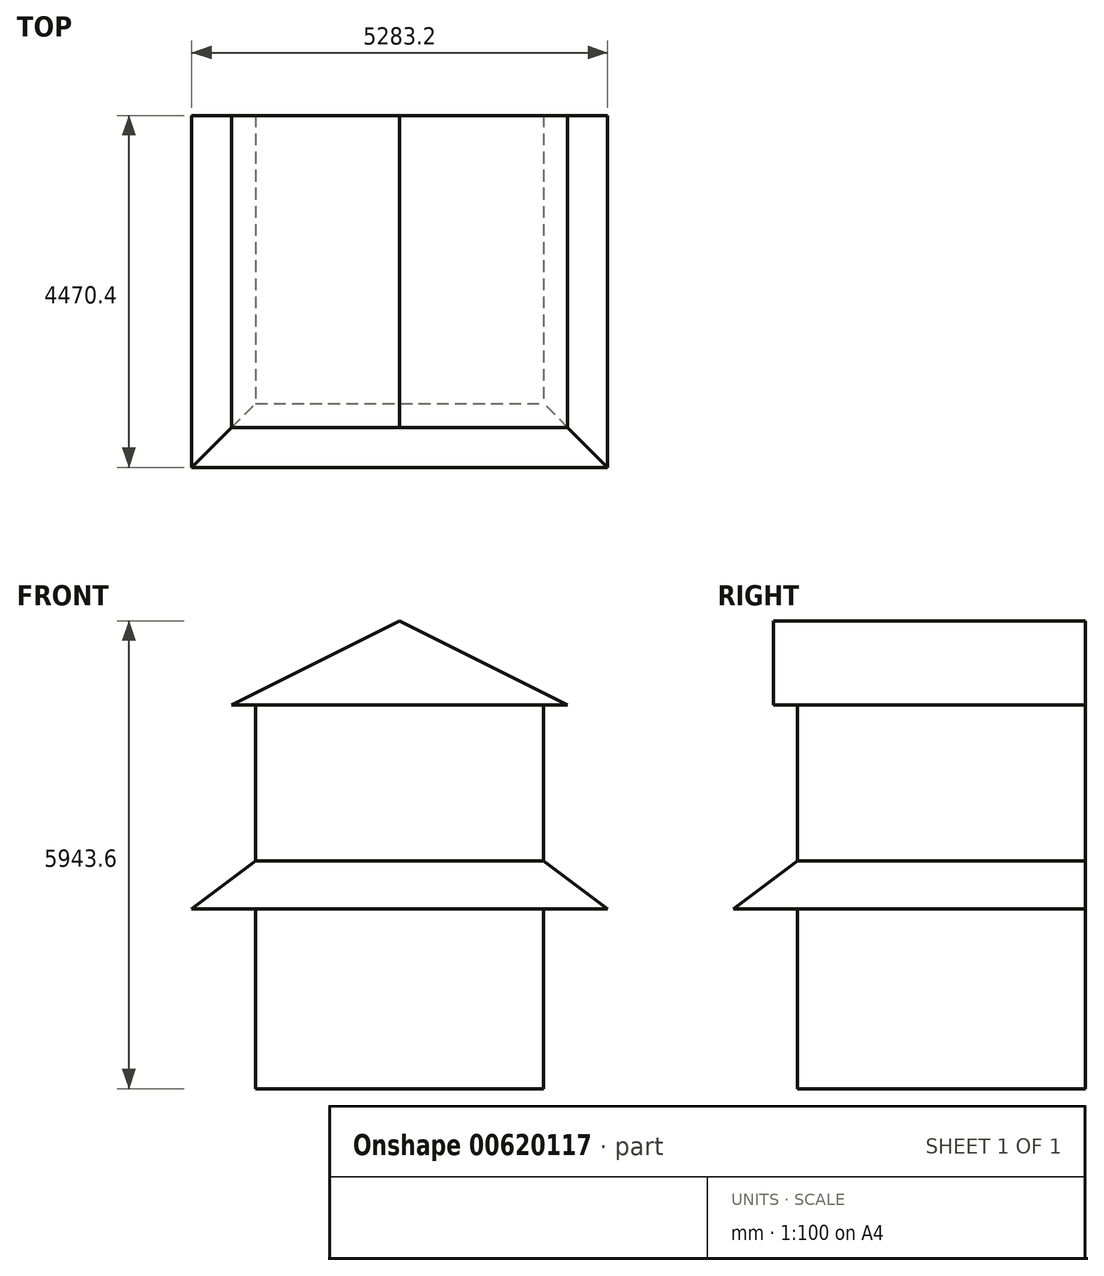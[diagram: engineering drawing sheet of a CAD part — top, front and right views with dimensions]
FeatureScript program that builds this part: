
annotation { "Feature Type Name" : "Feature", "Feature Type Description" : "" }
export const myFeature = defineFeature(function(context is Context, id is Id, definition is map)
    precondition{}
    {
        {
            var Q0;
            Q0=qCreatedBy(makeId("Top.planeOp"),FACE);
            var sketch = newSketch(context, id + "F0", { "sketchPlane" : qUnion([Q0])});
            skLineSegment(sketch, "E0.bottom", {"start": v(-1828.8, 1828.8) * mm, "end": v(1828.8, 1828.8) * mm});
            skLineSegment(sketch, "E0.top", {"start": v(-1828.8, -1828.8) * mm, "end": v(1828.8, -1828.8) * mm});
            skLineSegment(sketch, "E0.left", {"start": v(-1828.8, 1828.8) * mm, "end": v(-1828.8, -1828.8) * mm});
            skLineSegment(sketch, "E0.right", {"start": v(1828.8, 1828.8) * mm, "end": v(1828.8, -1828.8) * mm});
            skLineSegment(sketch, "E1", {"start": v(1828.8, 1828.8) * mm, "end": v(-1828.8, -1828.8) * mm, "construction": true});
            skSolve(sketch);
        }
        {
            var Q0;
            Q0=makeQuery(id+"F0.imprint","IMPRINT",FACE,{"disambiguationData":[TD([[makeQuery(id+"F0.imprint","IMPRINT",EDGE,{"derivedFrom":sQuery(id+"F0.wireOp",EDGE,"E0.bottom")}),-1.0]])]});
            extrude(context, id + "F1", {"entities" : qUnion([Q0]), "depth" : 4876.8 * mm, "offsetDistance" : 25.4 * mm});
        }
        {
            var Q0;
            Q0=makeQuery(id+"F1.opExtrude","SWEPT_FACE",FACE,{"disambiguationData":[OSD([sQuery(id+"F0.wireOp",EDGE,"E0.top")])]});
            var sketch = newSketch(context, id + "F2", { "sketchPlane" : qUnion([Q0])});
            skLineSegment(sketch, "E2.0", {"start": v(-2133.6, 4876.8) * mm, "end": v(2133.6, 4876.8) * mm});
            skLineSegment(sketch, "E3", {"start": v(-2133.6, 4876.8) * mm, "end": v(0, 5943.6) * mm});
            skLineSegment(sketch, "E4", {"start": v(0, 5943.6) * mm, "end": v(2133.6, 4876.8) * mm});
            skSolve(sketch);
        }
        {
            var Q0;
            Q0 = qSketchRegion(id + "F2", true);
            var Q1;
            Q1=makeQuery(id+"F1.opExtrude","SWEPT_FACE",FACE,{"disambiguationData":[OSD([sQuery(id+"F0.wireOp",EDGE,"E0.bottom")])]});
            extrude(context, id + "F3", {"entities" : qUnion([Q0]), "operationType" : NewBodyOperationType.ADD, "depth" : 304.8 * mm, "offsetDistance" : 25.4 * mm, "hasSecondDirection" : true, "secondDirectionBound" : BoundingType.UP_TO_SURFACE, "secondDirectionOppositeDirection" : true, "secondDirectionDepth" : 25.4 * mm, "secondDirectionBoundEntityFace" : qUnion([Q1])});
        }
        {
            var Q0;
            Q0=makeQuery(id+"F1.opExtrude","SWEPT_FACE",FACE,{"disambiguationData":[OSD([sQuery(id+"F0.wireOp",EDGE,"E0.top")])]});
            var sketch = newSketch(context, id + "F4", { "sketchPlane" : qUnion([Q0])});
            skLineSegment(sketch, "E5", {"start": v(-1828.8, 2895.6) * mm, "end": v(-1828.8, 2286) * mm});
            skLineSegment(sketch, "E6", {"start": v(-1828.8, 2286) * mm, "end": v(-2641.6, 2286) * mm});
            skLineSegment(sketch, "E7", {"start": v(-2641.6, 2286) * mm, "end": v(-1828.8, 2895.6) * mm});
            skLineSegment(sketch, "E8", {"start": v(0, 0) * mm, "end": v(0, 3018.86) * mm, "construction": true});
            skPoint(sketch, "E8.endSnap0", {"position": v(0, 0) * mm});
            skLineSegment(sketch, "E9.MirrorCS", {"start": v(1828.8, 2895.6) * mm, "end": v(1828.8, 2286) * mm});
            skLineSegment(sketch, "E10.MirrorCS", {"start": v(1828.8, 2286) * mm, "end": v(2641.6, 2286) * mm});
            skLineSegment(sketch, "E11.MirrorCS", {"start": v(2641.6, 2286) * mm, "end": v(1828.8, 2895.6) * mm});
            skSolve(sketch);
        }
        {
            var Q0;
            Q0 = qSketchRegion(id + "F4", true);
            var Q1;
            {var subQ0=sQuery(id+"F0.wireOp",EDGE,"E0.bottom");Q1=makeQuery(id+"F3.boolean.opBoolean","MERGE",FACE,{"derivedFrom":[makeQuery(id+"F1.opExtrude","SWEPT_FACE",FACE,{"disambiguationData":[OSD([subQ0])]}),makeQuery(id+"F3.opExtrude","CAP_FACE",FACE,{"disambiguationData":[OSD([subQ0])],"isStart":true})]});}
            extrude(context, id + "F5", {"entities" : qUnion([Q0]), "operationType" : NewBodyOperationType.ADD, "endBound" : BoundingType.UP_TO_SURFACE, "oppositeDirection" : true, "depth" : 25.4 * mm, "endBoundEntityFace" : qUnion([Q1]), "offsetDistance" : 25.4 * mm, "hasSecondDirection" : true, "secondDirectionOppositeDirection" : false, "secondDirectionDepth" : 1092.2 * mm});
        }
        {
            var Q0;
            {var subQ1=sQuery(id+"F0.wireOp",EDGE,"E0.left");var subQ3=sQuery(id+"F4.wireOp",EDGE,"E6");Q0=makeQuery(id+"F5.boolean.opBoolean","SPLIT",FACE,{"disambiguationData":[TD([makeQuery(id+"F5.opExtrude","SWEPT_FACE",FACE,{"disambiguationData":[OSD([subQ3])]})])],"derivedFrom":makeQuery(id+"F1.opExtrude","SWEPT_FACE",FACE,{"disambiguationData":[OSD([subQ1])]})});}
            var sketch = newSketch(context, id + "F6", { "sketchPlane" : qUnion([Q0])});
            skLineSegment(sketch, "E12", {"start": v(1828.8, 2286) * mm, "end": v(2641.6, 2286) * mm});
            skLineSegment(sketch, "E13", {"start": v(2641.6, 2286) * mm, "end": v(1828.8, 2895.6) * mm});
            skLineSegment(sketch, "E14", {"start": v(1828.8, 2895.6) * mm, "end": v(1828.8, 2286) * mm});
            skSolve(sketch);
        }
        {
            var Q0;
            Q0 = qSketchRegion(id + "F6", true);
            extrude(context, id + "F7", {"entities" : qUnion([Q0]), "operationType" : NewBodyOperationType.ADD, "depth" : 871.22 * mm, "offsetDistance" : 25.4 * mm, "hasSecondDirection" : true, "secondDirectionOppositeDirection" : true, "secondDirectionDepth" : 4513.58 * mm});
        }
        {
            var Q0;
            Q0=makeQuery(id+"F7.opExtrude","CAP_FACE",FACE,{"disambiguationData":[OSD([sQuery(id+"F6.wireOp",EDGE,"E12"),sQuery(id+"F6.wireOp",EDGE,"E13"),sQuery(id+"F6.wireOp",EDGE,"E14")])],"isStart":false});
            var sketch = newSketch(context, id + "F8", { "sketchPlane" : qUnion([Q0])});
            skLineSegment(sketch, "E15", {"start": v(1828.8, 2895.6) * mm, "end": v(2641.6, 2286) * mm});
            skLineSegment(sketch, "E16", {"start": v(2641.6, 2286) * mm, "end": v(3195.67, 2286) * mm});
            skLineSegment(sketch, "E17", {"start": v(3195.67, 2286) * mm, "end": v(3195.67, 2895.6) * mm});
            skLineSegment(sketch, "E18", {"start": v(3195.67, 2895.6) * mm, "end": v(1828.8, 2895.6) * mm});
            skSolve(sketch);
        }
        {
            var Q0;
            Q0 = qSketchRegion(id + "F8", true);
            extrude(context, id + "F9", {"entities" : qUnion([Q0]), "operationType" : NewBodyOperationType.REMOVE, "endBound" : BoundingType.THROUGH_ALL, "oppositeDirection" : true, "depth" : 25.4 * mm, "offsetDistance" : 25.4 * mm});
        }
        {
            var Q0;
            {var subQ0=sQuery(id+"F0.wireOp",EDGE,"E0.bottom");Q0=makeQuery(id+"F5.boolean.opBoolean","MERGE",FACE,{"derivedFrom":[makeQuery(id+"F3.boolean.opBoolean","MERGE",FACE,{"derivedFrom":[makeQuery(id+"F1.opExtrude","SWEPT_FACE",FACE,{"disambiguationData":[OSD([subQ0])]}),makeQuery(id+"F3.opExtrude","CAP_FACE",FACE,{"disambiguationData":[OSD([subQ0])],"isStart":true})]}),makeQuery(id+"F5.opExtrude","CAP_FACE",FACE,{"disambiguationData":[OSD([subQ0]),OD(0.0)],"isStart":false}),makeQuery(id+"F5.opExtrude","CAP_FACE",FACE,{"disambiguationData":[OSD([subQ0]),OD(1.0)],"isStart":false})]});}
            var sketch = newSketch(context, id + "F10", { "sketchPlane" : qUnion([Q0])});
            skLineSegment(sketch, "E19", {"start": v(-1828.8, 2895.6) * mm, "end": v(-2902.58, 2895.6) * mm});
            skLineSegment(sketch, "E20", {"start": v(-2902.58, 2895.6) * mm, "end": v(-2902.58, 2286) * mm});
            skLineSegment(sketch, "E21", {"start": v(-1828.8, 2895.6) * mm, "end": v(-2641.6, 2286) * mm});
            skLineSegment(sketch, "E22", {"start": v(-2641.6, 2286) * mm, "end": v(-2902.58, 2286) * mm});
            skLineSegment(sketch, "E23", {"start": v(0, 0) * mm, "end": v(0, 3784.62) * mm, "construction": true});
            skLineSegment(sketch, "E24.MirrorCS", {"start": v(2902.58, 2895.6) * mm, "end": v(2902.58, 2286) * mm});
            skLineSegment(sketch, "E25.MirrorCS", {"start": v(1828.8, 2895.6) * mm, "end": v(2641.6, 2286) * mm});
            skLineSegment(sketch, "E26.MirrorCS", {"start": v(1828.8, 2895.6) * mm, "end": v(2902.58, 2895.6) * mm});
            skLineSegment(sketch, "E27.MirrorCS", {"start": v(2641.6, 2286) * mm, "end": v(2902.58, 2286) * mm});
            skSolve(sketch);
        }
        {
            var Q0;
            Q0 = qSketchRegion(id + "F10", true);
            extrude(context, id + "F11", {"entities" : qUnion([Q0]), "operationType" : NewBodyOperationType.REMOVE, "endBound" : BoundingType.THROUGH_ALL, "oppositeDirection" : true, "depth" : 25.4 * mm, "offsetDistance" : 25.4 * mm});
        }
    });
